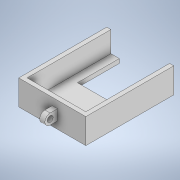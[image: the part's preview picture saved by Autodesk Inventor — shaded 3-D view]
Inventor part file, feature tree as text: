
AUTODESK INVENTOR PART (.ipt)
format: ipt  version: 2020.3 (Build 243373000, 373)  size: 160,256 bytes
history: native  units: mm
features: extrude x5, sketch x5, fillet x1
ambient origin geometry x8: Origin, YZ Plane, XZ Plane, XY Plane, X Axis, Y Axis, Z Axis, Center Point
bodies: Solid1 (feature_tree)
feature tree (11):
  extrude  "Extrusion1"  Depth=42.0mm
  extrude  "Extrusion2"  Depth=2.0mm
  extrude  "Extrusion3"  Depth=2.0mm
  extrude  "Extrusion4"  Depth=10.0mm TaperAngle=0.0deg
  extrude  "Extrusion5"  Depth=4.0mm
  fillet  "Fillet1"  Radius=4.0mm
  sketch  "Sketch1"  dims[d0=32.0mm d1=42.0mm]
  sketch  "Sketch2"  dims[d2=2.0mm d3=0.0mm d4=2.0mm]
  sketch  "Sketch3"  dims[d5=2.0mm d6=2.0mm]
  sketch  "Sketch4"  dims[d7=2.0mm d8=10.0mm d9=0.0mm]
  sketch  "Sketch5"  dims[d10=4.0mm d11=4.0mm d12=4.0mm d13=4.0mm d14=20.0mm d15=20.0mm d16=10.0mm d17=0.0mm d18=13.5mm d19=3.5mm d20=5.0mm d21=5.0mm d22=6.0mm d23=0.0mm d24=2.5mm d25=2.5mm d26=2.8mm d27=16.0mm d28=0.0mm d29=2.5mm]
